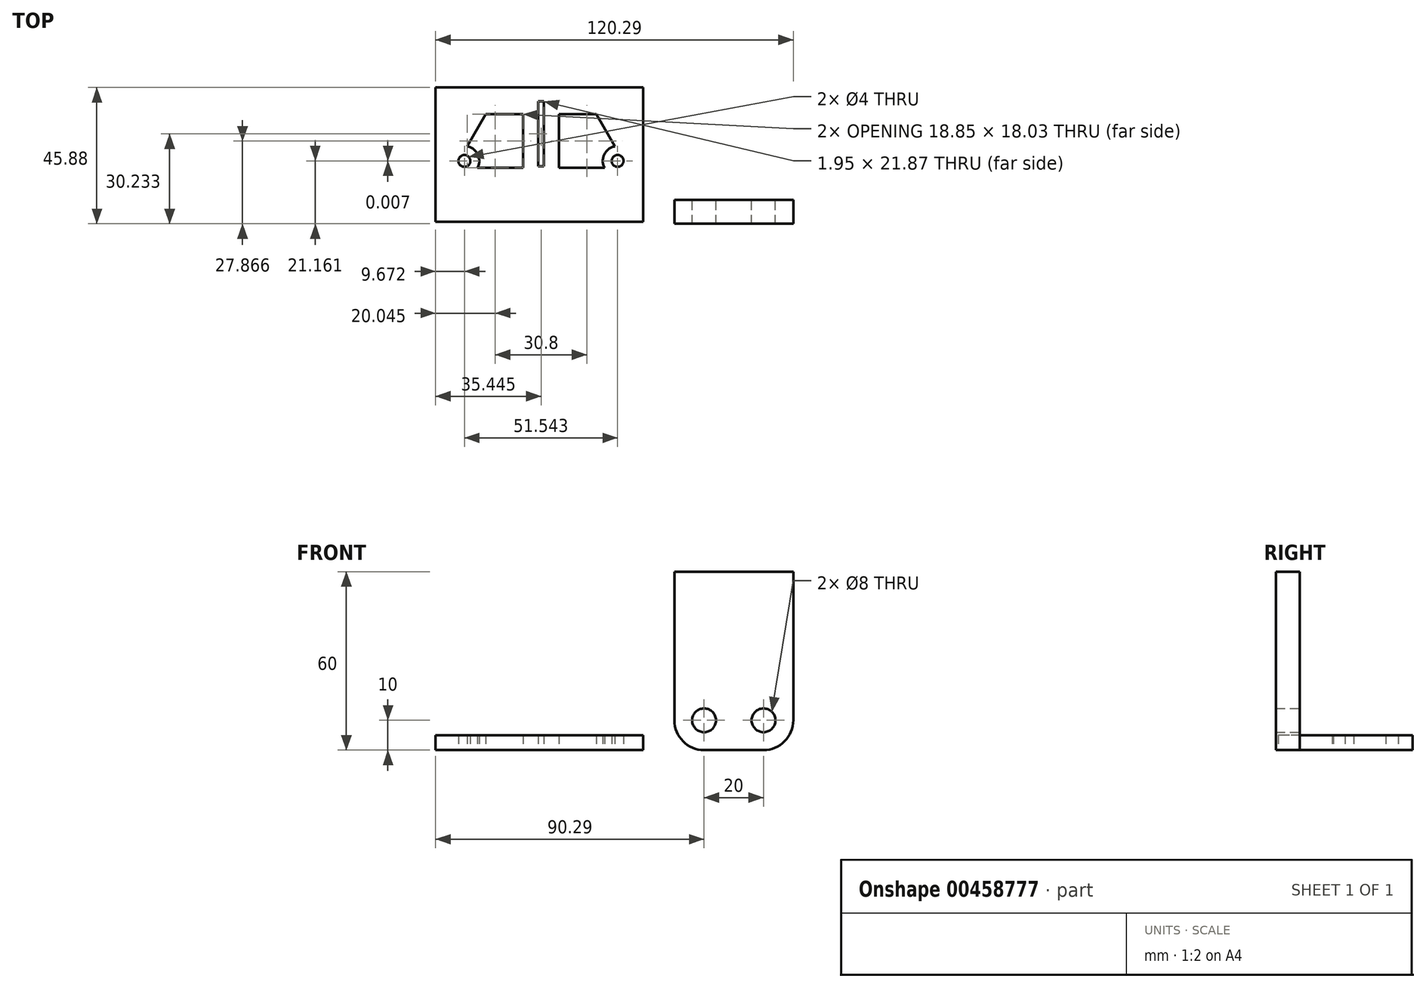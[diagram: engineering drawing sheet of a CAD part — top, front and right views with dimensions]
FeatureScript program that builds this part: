
annotation { "Feature Type Name" : "Feature", "Feature Type Description" : "" }
export const myFeature = defineFeature(function(context is Context, id is Id, definition is map)
    precondition{}
    {
        {
            var Q0;
            Q0=qCreatedBy(makeId("Front.planeOp"),FACE);
            var sketch = newSketch(context, id + "F0", { "sketchPlane" : qUnion([Q0])});
            skLineSegment(sketch, "E0", {"start": v(10, 0) * mm, "end": v(30, 0) * mm});
            skLineSegment(sketch, "E1", {"start": v(40, 10) * mm, "end": v(40, 60) * mm});
            skLineSegment(sketch, "E2", {"start": v(40, 60) * mm, "end": v(0, 60) * mm});
            skLineSegment(sketch, "E3", {"start": v(0, 60) * mm, "end": v(0, 10) * mm});
            skCircle(sketch, "E4", {"center": v(10, 10) * mm, "radius": 4 * mm});
            skCircle(sketch, "E5", {"center": v(30, 10) * mm, "radius": 4 * mm});
            skPoint(sketch, "E6.visualSharp", {"position": v(0, 0) * mm});
            skArc(sketch, "E6.filletArc", {"start": v(0, 10) * mm, "mid": v(2.93, 2.93) * mm, "end": v(10, 0) * mm});
            skPoint(sketch, "E7.visualSharp", {"position": v(40, 0) * mm});
            skArc(sketch, "E7.filletArc", {"start": v(30, 0) * mm, "mid": v(37.07, 2.93) * mm, "end": v(40, 10) * mm});
            skSolve(sketch);
        }
        {
            var Q0;
            Q0 = qSketchRegion(id + "F0", true);
            extrude(context, id + "F1", {"entities" : qUnion([Q0]), "depth" : 8 * mm});
        }
        {
            var Q0;
            Q0=qCreatedBy(makeId("Top.planeOp"),FACE);
            var sketch = newSketch(context, id + "F2", { "sketchPlane" : qUnion([Q0])});
            skLineSegment(sketch, "E8", {"start": v(-10.49, 37.88) * mm, "end": v(-10.49, -7.26) * mm});
            skLineSegment(sketch, "E9", {"start": v(-10.49, 37.88) * mm, "end": v(-80.29, 37.88) * mm});
            skLineSegment(sketch, "E10", {"start": v(-80.29, 37.88) * mm, "end": v(-80.29, -7.26) * mm});
            skLineSegment(sketch, "E11", {"start": v(-80.29, -7.26) * mm, "end": v(-10.49, -7.26) * mm});
            skLineSegment(sketch, "E12", {"start": v(-64.84, 33.17) * mm, "end": v(-24.84, 33.17) * mm});
            skLineSegment(sketch, "E13", {"start": v(-64.84, 33.17) * mm, "end": v(-74.95, 15.67) * mm});
            skLineSegment(sketch, "E14", {"start": v(-70.62, 8.17) * mm, "end": v(-19.08, 8.17) * mm});
            skLineSegment(sketch, "E15", {"start": v(-14.74, 15.67) * mm, "end": v(-24.84, 33.17) * mm});
            skCircle(sketch, "E16", {"center": v(-70.62, 13.17) * mm, "radius": 2 * mm});
            skArc(sketch, "E17", {"start": v(-74.95, 15.67) * mm, "mid": v(-74.95, 10.67) * mm, "end": v(-70.62, 8.17) * mm});
            skLineSegment(sketch, "E18", {"start": v(-66.19, 10.85) * mm, "end": v(-50.82, 10.85) * mm});
            skLineSegment(sketch, "E19", {"start": v(-50.82, 10.85) * mm, "end": v(-50.82, 28.88) * mm});
            skLineSegment(sketch, "E20", {"start": v(-50.82, 28.88) * mm, "end": v(-63.43, 28.88) * mm});
            skLineSegment(sketch, "E21", {"start": v(-63.43, 28.88) * mm, "end": v(-69.67, 18.08) * mm});
            skArc(sketch, "E22.trimOffspring", {"start": v(-66.19, 10.85) * mm, "mid": v(-66.11, 15.34) * mm, "end": v(-69.67, 18.08) * mm});
            skCircle(sketch, "E23.MirrorC", {"center": v(-19.07, 13.16) * mm, "radius": 2 * mm});
            skLineSegment(sketch, "E24", {"start": v(-44.84, 33.17) * mm, "end": v(-44.84, 8.17) * mm, "construction": true});
            skLineSegment(sketch, "E25.MirrorCS", {"start": v(-38.87, 10.85) * mm, "end": v(-38.87, 28.88) * mm});
            skLineSegment(sketch, "E26.MirrorCS", {"start": v(-38.87, 28.88) * mm, "end": v(-26.26, 28.88) * mm});
            skLineSegment(sketch, "E27.MirrorCS", {"start": v(-26.26, 28.88) * mm, "end": v(-20.02, 18.08) * mm});
            skArc(sketch, "E28.MirrorCS", {"start": v(-23.5, 10.85) * mm, "mid": v(-23.58, 15.34) * mm, "end": v(-20.02, 18.08) * mm});
            skLineSegment(sketch, "E29.MirrorCS", {"start": v(-23.5, 10.85) * mm, "end": v(-38.87, 10.85) * mm});
            skArc(sketch, "E30.MirrorCS", {"start": v(-14.74, 15.67) * mm, "mid": v(-14.74, 10.67) * mm, "end": v(-19.07, 8.17) * mm});
            skLineSegment(sketch, "E31", {"start": v(-45.82, 33.17) * mm, "end": v(-45.82, 11.3) * mm});
            skLineSegment(sketch, "E32", {"start": v(-45.82, 11.3) * mm, "end": v(-44.84, 11.3) * mm});
            skLineSegment(sketch, "E33", {"start": v(-44.84, 11.3) * mm, "end": v(-43.87, 11.3) * mm});
            skLineSegment(sketch, "E34", {"start": v(-43.87, 11.3) * mm, "end": v(-43.87, 33.17) * mm});
            skSolve(sketch);
        }
        {
            var Q0;
            Q0 = qSketchRegion(id + "F2", true);
            extrude(context, id + "F3", {"entities" : qUnion([Q0]), "depth" : 5 * mm});
        }
    });
